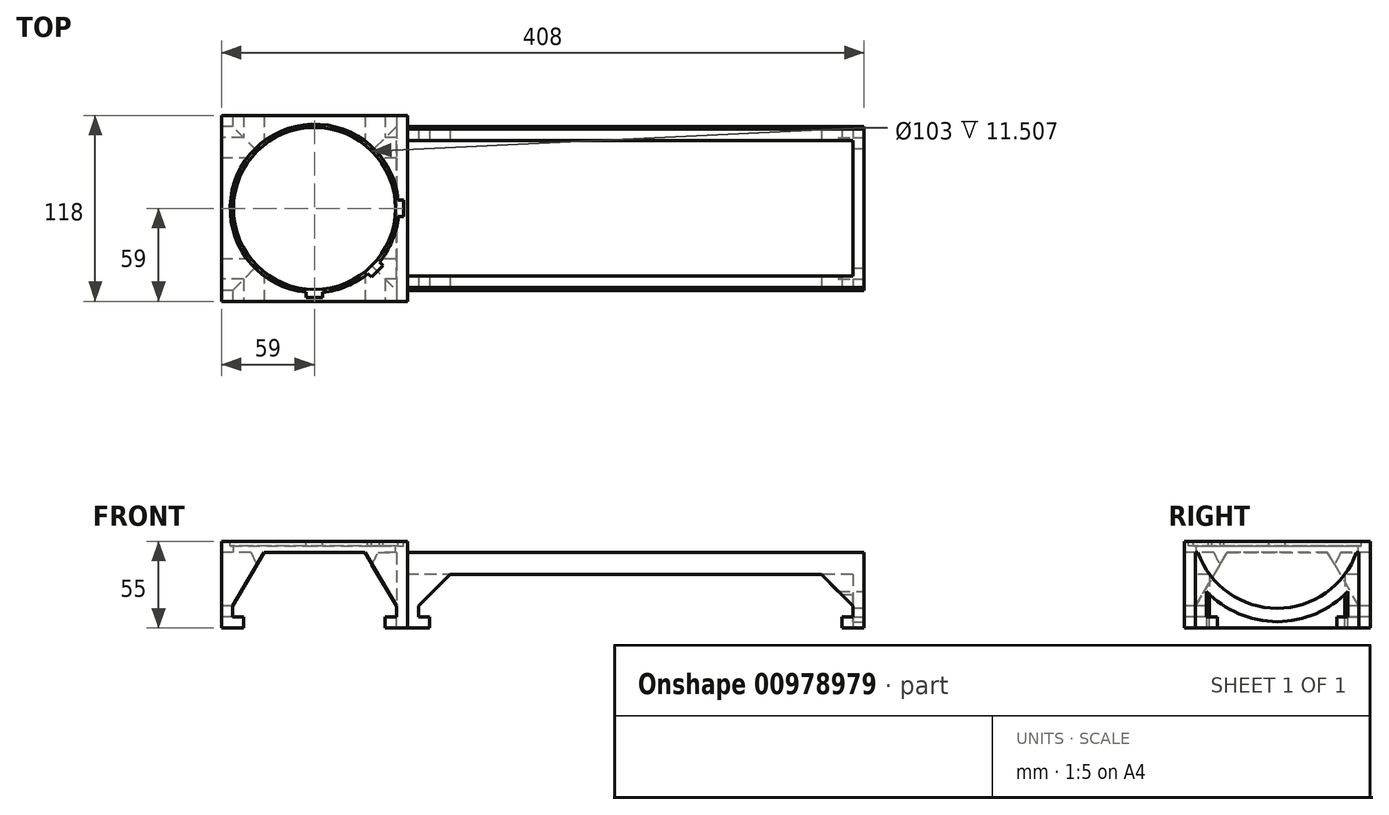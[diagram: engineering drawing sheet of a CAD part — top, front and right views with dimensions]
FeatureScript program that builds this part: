
annotation { "Feature Type Name" : "Feature", "Feature Type Description" : "" }
export const myFeature = defineFeature(function(context is Context, id is Id, definition is map)
    precondition{}
    {
        {
            var Q0;
            Q0=qCreatedBy(makeId("Top.planeOp"),FACE);
            var sketch = newSketch(context, id + "F0", { "sketchPlane" : qUnion([Q0])});
            skLineSegment(sketch, "E0.bottom", {"start": v(0, 0) * mm, "end": v(-118, 0) * mm});
            skLineSegment(sketch, "E0.top", {"start": v(0, 118) * mm, "end": v(-118, 118) * mm});
            skLineSegment(sketch, "E0.left", {"start": v(0, 0) * mm, "end": v(0, 118) * mm});
            skLineSegment(sketch, "E0.right", {"start": v(-118, 0) * mm, "end": v(-118, 118) * mm});
            skSolve(sketch);
        }
        {
            var Q0;
            Q0=makeQuery(id+"F0.imprint","IMPRINT",FACE,{"disambiguationData":[TD([[makeQuery(id+"F0.imprint","IMPRINT",EDGE,{"derivedFrom":sQuery(id+"F0.wireOp",EDGE,"E0.bottom")}),-1.0]])]});
            extrude(context, id + "F1", {"entities" : qUnion([Q0]), "depth" : 55 * mm, "offsetDistance" : 25 * mm});
        }
        {
            var Q0;
            Q0=makeQuery(id+"F1.opExtrude","CAP_FACE",FACE,{"disambiguationData":[OSD([sQuery(id+"F0.wireOp",EDGE,"E0.bottom"),sQuery(id+"F0.wireOp",EDGE,"E0.top"),sQuery(id+"F0.wireOp",EDGE,"E0.left"),sQuery(id+"F0.wireOp",EDGE,"E0.right")])],"isStart":false});
            var sketch = newSketch(context, id + "F2", { "sketchPlane" : qUnion([Q0])});
            skCircle(sketch, "E1", {"center": v(-59, 59) * mm, "radius": 53.5 * mm});
            skLineSegment(sketch, "E2", {"start": v(-59, 59) * mm, "end": v(-59, 5.5) * mm});
            skLineSegment(sketch, "E3", {"start": v(-59, 59) * mm, "end": v(-5.5, 59) * mm});
            skLineSegment(sketch, "E4", {"start": v(-64.3, 5.76) * mm, "end": v(-64.3, 2.46) * mm});
            skLineSegment(sketch, "E5", {"start": v(-64.3, 2.46) * mm, "end": v(-53.7, 2.46) * mm});
            skLineSegment(sketch, "E6", {"start": v(-53.7, 2.46) * mm, "end": v(-53.7, 5.76) * mm});
            skLineSegment(sketch, "E7", {"start": v(-5.76, 64.3) * mm, "end": v(-2.46, 64.3) * mm});
            skLineSegment(sketch, "E8", {"start": v(-2.46, 64.3) * mm, "end": v(-2.46, 53.7) * mm});
            skLineSegment(sketch, "E9", {"start": v(-2.46, 53.7) * mm, "end": v(-5.76, 53.7) * mm});
            skLineSegment(sketch, "E10", {"start": v(-59, 59) * mm, "end": v(-21.17, 21.17) * mm});
            skLineSegment(sketch, "E11", {"start": v(-25.1, 17.6) * mm, "end": v(-22.77, 15.27) * mm});
            skLineSegment(sketch, "E12", {"start": v(-22.77, 15.27) * mm, "end": v(-15.27, 22.77) * mm});
            skLineSegment(sketch, "E13", {"start": v(-15.27, 22.77) * mm, "end": v(-17.6, 25.1) * mm});
            skSolve(sketch);
        }
        {
            var Q0;
            {var subQ0=sQuery(id+"F2.wireOp",EDGE,"E2");Q0=makeQuery(id+"F2.imprint","IMPRINT",FACE,{"disambiguationData":[TD([[makeQuery(id+"F2.imprint","IMPRINT",EDGE,{"derivedFrom":subQ0}),-1.0]])]});}
            var Q1;
            {var subQ0=sQuery(id+"F2.wireOp",EDGE,"E4");Q1=makeQuery(id+"F2.imprint","IMPRINT",FACE,{"disambiguationData":[TD([[makeQuery(id+"F2.imprint","IMPRINT",EDGE,{"derivedFrom":subQ0}),1.0]])]});}
            var Q2;
            {var subQ3=sQuery(id+"F2.wireOp",EDGE,"E2");Q2=makeQuery(id+"F2.imprint","IMPRINT",FACE,{"disambiguationData":[TD([[makeQuery(id+"F2.imprint","IMPRINT",EDGE,{"derivedFrom":subQ3}),1.0]])]});}
            var Q3;
            {var subQ0=sQuery(id+"F2.wireOp",EDGE,"E11");Q3=makeQuery(id+"F2.imprint","IMPRINT",FACE,{"disambiguationData":[TD([[makeQuery(id+"F2.imprint","IMPRINT",EDGE,{"derivedFrom":subQ0}),1.0]])]});}
            var Q4;
            {var subQ0=sQuery(id+"F2.wireOp",EDGE,"E3");Q4=makeQuery(id+"F2.imprint","IMPRINT",FACE,{"disambiguationData":[TD([[makeQuery(id+"F2.imprint","IMPRINT",EDGE,{"derivedFrom":subQ0}),-1.0]])]});}
            var Q5;
            {var subQ0=sQuery(id+"F2.wireOp",EDGE,"E7");Q5=makeQuery(id+"F2.imprint","IMPRINT",FACE,{"disambiguationData":[TD([[makeQuery(id+"F2.imprint","IMPRINT",EDGE,{"derivedFrom":subQ0}),-1.0]])]});}
            extrude(context, id + "F3", {"entities" : qUnion([Q0, Q1, Q2, Q3, Q4, Q5]), "operationType" : NewBodyOperationType.REMOVE, "oppositeDirection" : true, "depth" : 3 * mm, "offsetDistance" : 25 * mm});
        }
        {
            var Q0;
            Q0=makeQuery(id+"F3.boolean.opBoolean","COPY",FACE,{"derivedFrom":makeQuery(id+"F3.opExtrude","CAP_FACE",FACE,{"disambiguationData":[OSD([sQuery(id+"F2.wireOp",EDGE,"E1"),sQuery(id+"F2.wireOp",EDGE,"E4"),sQuery(id+"F2.wireOp",EDGE,"E5"),sQuery(id+"F2.wireOp",EDGE,"E6"),sQuery(id+"F2.wireOp",EDGE,"E7"),sQuery(id+"F2.wireOp",EDGE,"E8"),sQuery(id+"F2.wireOp",EDGE,"E9"),sQuery(id+"F2.wireOp",EDGE,"E11"),sQuery(id+"F2.wireOp",EDGE,"E12"),sQuery(id+"F2.wireOp",EDGE,"E13")])],"isStart":false})});
            var sketch = newSketch(context, id + "F4", { "sketchPlane" : qUnion([Q0])});
            skCircle(sketch, "E14", {"center": v(-59, 59) * mm, "radius": 51.5 * mm});
            skSolve(sketch);
        }
        {
            var Q0;
            Q0=makeQuery(id+"F4.imprint","IMPRINT",FACE,{"disambiguationData":[TD([[makeQuery(id+"F4.imprint","IMPRINT",EDGE,{"derivedFrom":sQuery(id+"F4.wireOp",EDGE,"E14")}),1.0]])]});
            extrude(context, id + "F5", {"entities" : qUnion([Q0]), "operationType" : NewBodyOperationType.REMOVE, "oppositeDirection" : true, "depth" : 100 * mm, "offsetDistance" : 25 * mm});
        }
        {
            var Q0;
            Q0=makeQuery(id+"F1.opExtrude","SWEPT_FACE",FACE,{"disambiguationData":[OSD([sQuery(id+"F0.wireOp",EDGE,"E0.bottom")])]});
            var sketch = newSketch(context, id + "F6", { "sketchPlane" : qUnion([Q0])});
            skLineSegment(sketch, "E15", {"start": v(-104, 0) * mm, "end": v(-104, 7) * mm});
            skLineSegment(sketch, "E16", {"start": v(-104, 7) * mm, "end": v(-111, 7) * mm});
            skLineSegment(sketch, "E17", {"start": v(-111, 7) * mm, "end": v(-111, 14) * mm});
            skLineSegment(sketch, "E18", {"start": v(-111, 14) * mm, "end": v(-91, 48) * mm});
            skLineSegment(sketch, "E19", {"start": v(-91, 48) * mm, "end": v(-27, 48) * mm});
            skLineSegment(sketch, "E20", {"start": v(-27, 48) * mm, "end": v(-7, 14) * mm});
            skLineSegment(sketch, "E21", {"start": v(-7, 14) * mm, "end": v(-7, 7) * mm});
            skLineSegment(sketch, "E22", {"start": v(-7, 7) * mm, "end": v(-14, 7) * mm});
            skLineSegment(sketch, "E23", {"start": v(-14, 7) * mm, "end": v(-14, 0) * mm});
            skSolve(sketch);
        }
        {
            var Q0;
            {var subQ0=sQuery(id+"F6.wireOp",EDGE,"E15");Q0=makeQuery(id+"F6.imprint","IMPRINT",FACE,{"disambiguationData":[TD([[makeQuery(id+"F6.imprint","IMPRINT",EDGE,{"derivedFrom":subQ0}),-1.0]])]});}
            extrude(context, id + "F7", {"entities" : qUnion([Q0]), "operationType" : NewBodyOperationType.REMOVE, "oppositeDirection" : true, "depth" : 150 * mm, "offsetDistance" : 25 * mm});
        }
        {
            var Q0;
            Q0=makeQuery(id+"F1.opExtrude","SWEPT_FACE",FACE,{"disambiguationData":[OSD([sQuery(id+"F0.wireOp",EDGE,"E0.right")])]});
            var sketch = newSketch(context, id + "F8", { "sketchPlane" : qUnion([Q0])});
            skLineSegment(sketch, "E24", {"start": v(-104, 0) * mm, "end": v(-104, 7) * mm});
            skLineSegment(sketch, "E25", {"start": v(-104, 7) * mm, "end": v(-111, 7) * mm});
            skLineSegment(sketch, "E26", {"start": v(-111, 7) * mm, "end": v(-111, 14) * mm});
            skLineSegment(sketch, "E27", {"start": v(-111, 14) * mm, "end": v(-91, 48) * mm});
            skLineSegment(sketch, "E28", {"start": v(-91, 48) * mm, "end": v(-27, 48) * mm});
            skLineSegment(sketch, "E29", {"start": v(-27, 48) * mm, "end": v(-7, 14) * mm});
            skLineSegment(sketch, "E30", {"start": v(-7, 14) * mm, "end": v(-7, 7) * mm});
            skLineSegment(sketch, "E31", {"start": v(-7, 7) * mm, "end": v(-14, 7) * mm});
            skLineSegment(sketch, "E32", {"start": v(-14, 7) * mm, "end": v(-14, 0) * mm});
            skSolve(sketch);
        }
        {
            var Q0;
            {var subQ0=sQuery(id+"F8.wireOp",EDGE,"E24");Q0=makeQuery(id+"F8.imprint","IMPRINT",FACE,{"disambiguationData":[TD([[makeQuery(id+"F8.imprint","IMPRINT",EDGE,{"derivedFrom":subQ0}),-1.0]])]});}
            extrude(context, id + "F9", {"entities" : qUnion([Q0]), "operationType" : NewBodyOperationType.REMOVE, "oppositeDirection" : true, "depth" : 111 * mm, "offsetDistance" : 25 * mm});
        }
        {
            var Q0;
            Q0=makeQuery(id+"F1.opExtrude","SWEPT_FACE",FACE,{"disambiguationData":[OSD([sQuery(id+"F0.wireOp",EDGE,"E0.left")])]});
            var sketch = newSketch(context, id + "F10", { "sketchPlane" : qUnion([Q0])});
            skLineSegment(sketch, "E33.bottom", {"start": v(7, 0) * mm, "end": v(111, 0) * mm});
            skLineSegment(sketch, "E33.top", {"start": v(7, 48) * mm, "end": v(111, 48) * mm});
            skLineSegment(sketch, "E33.left", {"start": v(7, 0) * mm, "end": v(7, 48) * mm});
            skLineSegment(sketch, "E33.right", {"start": v(111, 0) * mm, "end": v(111, 48) * mm});
            skCircle(sketch, "E34", {"center": v(59, 66) * mm, "radius": 53.5 * mm});
            skLineSegment(sketch, "E35.bottom", {"start": v(27.75, 30) * mm, "end": v(91.25, 30) * mm});
            skLineSegment(sketch, "E35.top", {"start": v(27.75, 27) * mm, "end": v(91.25, 27) * mm});
            skLineSegment(sketch, "E35.left", {"start": v(27.75, 30) * mm, "end": v(27.75, 27) * mm});
            skLineSegment(sketch, "E35.right", {"start": v(91.25, 30) * mm, "end": v(91.25, 27) * mm});
            skLineSegment(sketch, "E36.bottom", {"start": v(29.25, 30) * mm, "end": v(88.75, 30) * mm});
            skLineSegment(sketch, "E36.top", {"start": v(29.25, 73) * mm, "end": v(88.75, 73) * mm});
            skLineSegment(sketch, "E36.left", {"start": v(29.25, 30) * mm, "end": v(29.25, 73) * mm});
            skLineSegment(sketch, "E36.right", {"start": v(88.75, 30) * mm, "end": v(88.75, 73) * mm});
            skSolve(sketch);
        }
        {
            var Q0;
            Q0=makeQuery(id+"F10.imprint","IMPRINT",FACE,{"disambiguationData":[TD([[makeQuery(id+"F10.imprint","IMPRINT",EDGE,{"derivedFrom":sQuery(id+"F10.wireOp",EDGE,"E33.bottom")}),1.0]])]});
            extrude(context, id + "F11", {"entities" : qUnion([Q0]), "operationType" : NewBodyOperationType.ADD, "depth" : 290 * mm, "offsetDistance" : 25 * mm});
        }
        {
            var Q0;
            {var subQ0=sQuery(id+"F0.wireOp",EDGE,"E0.left");var subQ1=sQuery(id+"F0.wireOp",EDGE,"E0.top");var subQ2=sQuery(id+"F0.wireOp",EDGE,"E0.bottom");Q0=makeQuery(id+"F11.boolean.opBoolean","MERGE",FACE,{"derivedFrom":[makeQuery(id+"F7.boolean.opBoolean","SPLIT",FACE,{"disambiguationData":[TD([makeQuery(id+"F1.opExtrude","SWEPT_FACE",FACE,{"disambiguationData":[OSD([subQ0])]})])],"derivedFrom":makeQuery(id+"F1.opExtrude","CAP_FACE",FACE,{"disambiguationData":[OSD([subQ2,subQ1,subQ0,sQuery(id+"F0.wireOp",EDGE,"E0.right")])],"isStart":true})}),makeQuery(id+"F11.opExtrude","SWEPT_FACE",FACE,{"disambiguationData":[OSD([sQuery(id+"F10.wireOp",EDGE,"E33.bottom")])]})]});}
            var sketch = newSketch(context, id + "F12", { "sketchPlane" : qUnion([Q0])});
            skLineSegment(sketch, "E37.bottom", {"start": v(283, -16) * mm, "end": v(0, -16) * mm});
            skLineSegment(sketch, "E37.top", {"start": v(283, -102) * mm, "end": v(0, -102) * mm});
            skLineSegment(sketch, "E37.left", {"start": v(283, -16) * mm, "end": v(283, -102) * mm});
            skLineSegment(sketch, "E37.right", {"start": v(0, -16) * mm, "end": v(0, -102) * mm});
            skSolve(sketch);
        }
        {
            var Q0;
            Q0=makeQuery(id+"F12.imprint","IMPRINT",FACE,{"disambiguationData":[TD([[makeQuery(id+"F12.imprint","IMPRINT",EDGE,{"derivedFrom":sQuery(id+"F12.wireOp",EDGE,"E37.bottom")}),1.0]])]});
            extrude(context, id + "F13", {"entities" : qUnion([Q0]), "operationType" : NewBodyOperationType.REMOVE, "oppositeDirection" : true, "depth" : 50 * mm, "offsetDistance" : 25 * mm});
        }
        {
            var Q0;
            Q0=makeQuery(id+"F11.opExtrude","SWEPT_FACE",FACE,{"disambiguationData":[OSD([sQuery(id+"F10.wireOp",EDGE,"E33.left")])]});
            var sketch = newSketch(context, id + "F14", { "sketchPlane" : qUnion([Q0])});
            skLineSegment(sketch, "E38", {"start": v(14, 0) * mm, "end": v(14, 7) * mm});
            skLineSegment(sketch, "E39", {"start": v(14, 7) * mm, "end": v(7, 7) * mm});
            skLineSegment(sketch, "E40", {"start": v(7, 7) * mm, "end": v(7, 14) * mm});
            skLineSegment(sketch, "E41", {"start": v(7, 14) * mm, "end": v(27, 34) * mm});
            skLineSegment(sketch, "E42", {"start": v(27, 34) * mm, "end": v(263, 34) * mm});
            skLineSegment(sketch, "E43", {"start": v(263, 34) * mm, "end": v(283, 14) * mm});
            skLineSegment(sketch, "E44", {"start": v(283, 14) * mm, "end": v(283, 7) * mm});
            skLineSegment(sketch, "E45", {"start": v(283, 7) * mm, "end": v(276, 7) * mm});
            skLineSegment(sketch, "E46", {"start": v(276, 7) * mm, "end": v(276, 0) * mm});
            skSolve(sketch);
        }
        {
            var Q0;
            {var subQ0=sQuery(id+"F14.wireOp",EDGE,"E38");Q0=makeQuery(id+"F14.imprint","IMPRINT",FACE,{"disambiguationData":[TD([[makeQuery(id+"F14.imprint","IMPRINT",EDGE,{"derivedFrom":subQ0}),-1.0]])]});}
            extrude(context, id + "F15", {"entities" : qUnion([Q0]), "operationType" : NewBodyOperationType.REMOVE, "oppositeDirection" : true, "depth" : 150 * mm, "offsetDistance" : 25 * mm});
        }
        {
            var Q0;
            Q0=makeQuery(id+"F11.opExtrude","CAP_FACE",FACE,{"disambiguationData":[OSD([sQuery(id+"F10.wireOp",EDGE,"E33.bottom"),sQuery(id+"F10.wireOp",EDGE,"E33.top"),sQuery(id+"F10.wireOp",EDGE,"E33.left"),sQuery(id+"F10.wireOp",EDGE,"E33.right"),sQuery(id+"F10.wireOp",EDGE,"E34")])],"isStart":false});
            var sketch = newSketch(context, id + "F16", { "sketchPlane" : qUnion([Q0])});
            skCircle(sketch, "E47", {"center": v(59, 66) * mm, "radius": 62 * mm});
            skLineSegment(sketch, "E48", {"start": v(97, 0) * mm, "end": v(97, 7) * mm});
            skLineSegment(sketch, "E49", {"start": v(97, 7) * mm, "end": v(104, 7) * mm});
            skLineSegment(sketch, "E50", {"start": v(104, 7) * mm, "end": v(104, 23.35) * mm});
            skLineSegment(sketch, "E51", {"start": v(21, 0) * mm, "end": v(21, 7) * mm});
            skLineSegment(sketch, "E52", {"start": v(21, 7) * mm, "end": v(14, 7) * mm});
            skLineSegment(sketch, "E53", {"start": v(14, 7) * mm, "end": v(14, 23.35) * mm});
            skSolve(sketch);
        }
        {
            var Q0;
            {var subQ0=sQuery(id+"F16.wireOp",EDGE,"E48");Q0=makeQuery(id+"F16.imprint","IMPRINT",FACE,{"disambiguationData":[TD([[makeQuery(id+"F16.imprint","IMPRINT",EDGE,{"derivedFrom":subQ0}),1.0]])]});}
            extrude(context, id + "F17", {"entities" : qUnion([Q0]), "operationType" : NewBodyOperationType.REMOVE, "oppositeDirection" : true, "depth" : 25 * mm, "offsetDistance" : 25 * mm});
        }
    });
